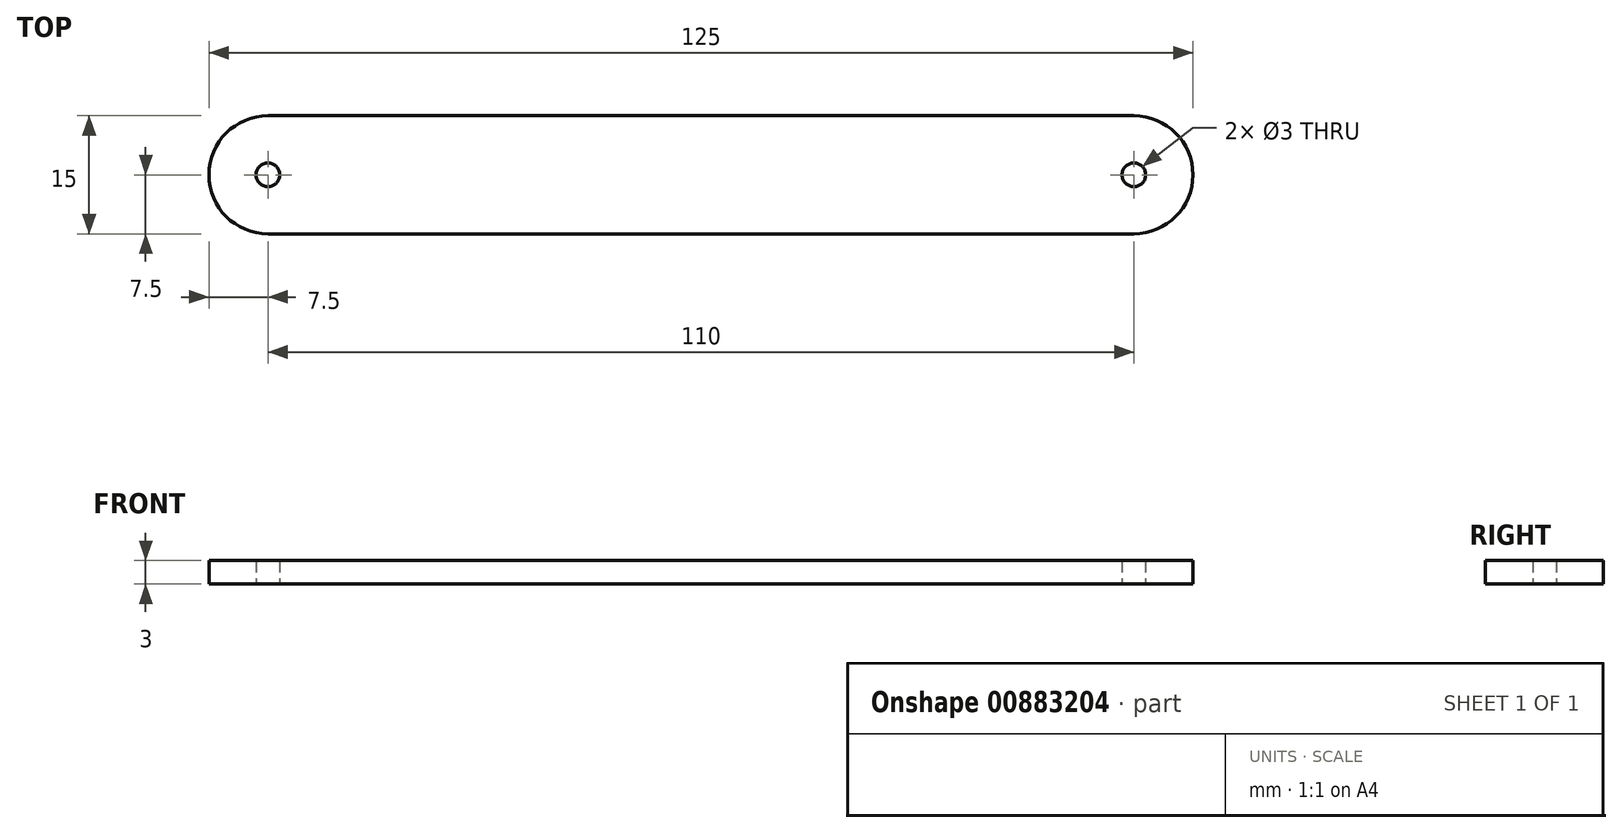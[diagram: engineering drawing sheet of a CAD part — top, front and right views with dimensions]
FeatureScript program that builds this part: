
annotation { "Feature Type Name" : "Feature", "Feature Type Description" : "" }
export const myFeature = defineFeature(function(context is Context, id is Id, definition is map)
    precondition{}
    {
        {
            var Q0;
            Q0=qCreatedBy(makeId("Top.planeOp"),FACE);
            var sketch = newSketch(context, id + "F0", { "sketchPlane" : qUnion([Q0])});
            skLineSegment(sketch, "E0.bottom", {"start": v(0, 0) * mm, "end": v(110, 0) * mm});
            skLineSegment(sketch, "E0.top", {"start": v(0, 15) * mm, "end": v(110, 15) * mm});
            skLineSegment(sketch, "E0.left", {"start": v(0, 0) * mm, "end": v(0, 15) * mm});
            skLineSegment(sketch, "E0.right", {"start": v(110, 0) * mm, "end": v(110, 15) * mm});
            skArc(sketch, "E1", {"start": v(110, 0) * mm, "mid": v(117.5, 7.5) * mm, "end": v(110, 15) * mm});
            skArc(sketch, "E2", {"start": v(0, 15) * mm, "mid": v(-7.5, 7.5) * mm, "end": v(0, 0) * mm});
            skCircle(sketch, "E3", {"center": v(0, 7.5) * mm, "radius": 1.5 * mm});
            skCircle(sketch, "E4", {"center": v(110, 7.5) * mm, "radius": 1.5 * mm});
            skSolve(sketch);
        }
        {
            var Q0;
            Q0 = qSketchRegion(id + "F0", true);
            extrude(context, id + "F1", {"entities" : qUnion([Q0]), "depth" : 3 * mm, "offsetDistance" : 25 * mm});
        }
    });
